# Revit family: HandDryer_SurfaceMount_ASIJDMacDonald_Applause
name_source: partatom
category: Specialty Equipment
revit_build: Autodesk Revit 2016 (Build: 20190508_0715(x64)
units: mm (PartAtom-declared; Revit-internal decimal feet)

## family parameters
Always vertical = Yes
Cut with Voids When Loaded = Yes
OmniClass Number = 23.40.20.21.14
OmniClass Title = Hand and Hair Dryers
Part Type = Normal
Room Calculation Point = No
Round Connector Dimension = Use Diameter
Shared = No
Work Plane-Based = No

## types (3) — shared parameters
Manufacturer = ASI JD MacDonald
Manufacturer_Overall Depth = 146 mm
Manufacturer_Overall Height = 361 mm
Manufacturer_Overall Width = 250 mm
Manufacturer_URL__Product Specific = https://jdmacdonald.com.au
ModifiedIssue_ANZRS = 20190912 $
Nozzle Material = z_ASI JD MacDonald_Plastic_Dark Grey
URL = www.asijdmacdonald.com.au
Voltage = 240 V
zero-valued in all types: Cost

## per-type parameters (varying)
| type | Body Material | Description | Manufacturer_Spec Code | Model | Type Comments |
| White (HDAPWHT) | z_ASI JD MacDonald_Steel_White Powder Coated | Applause Automatic Hand Dryer – White (HDAPWHT) | HDAPWHT | HDAPWHT | Hand Dryer - Surface Mount - Applause - White |
| Satin (HDAPSSS) | z_ASI JD MacDonald_Stainless Steel | Applause Automatic Hand Dryer – Satin Stainless Steel (HDAPSSS) | HDAPSSS | HDAPSSS | Hand Dryer - Surface Mount - Applause - Satin Stainless Steel |
| Polished (HDAPPSS) | z_ASI JD MacDonald_Stainless Steel_Polished | Applause Automatic Hand Dryer – Polished Stainless Steel (HDAPPSS) | HDAPPSS | HDAPPSS | Hand Dryer - Surface Mount - Applause - Polished Stainless Steel |

## geometry (parser evidence)
native form markers: Sweep x3
no freeform markers — native parametric forms only
